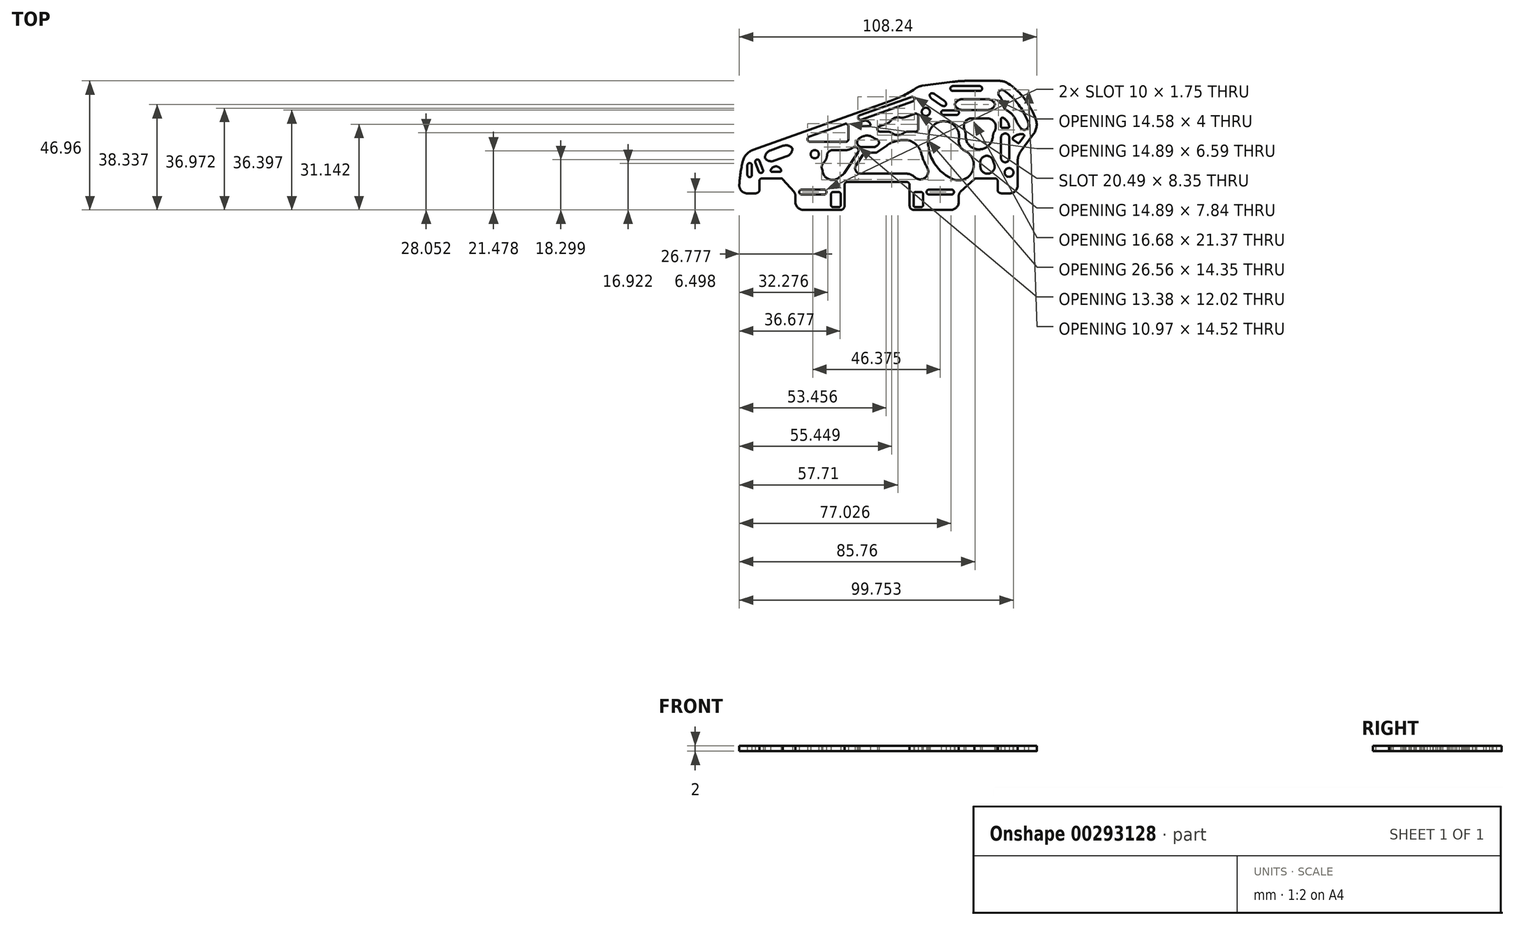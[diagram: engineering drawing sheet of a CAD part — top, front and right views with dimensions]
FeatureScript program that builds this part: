
annotation { "Feature Type Name" : "Feature", "Feature Type Description" : "" }
export const myFeature = defineFeature(function(context is Context, id is Id, definition is map)
    precondition{}
    {
        {
            var Q0;
            Q0=qCreatedBy(makeId("Top.planeOp"),FACE);
            var sketch = newSketch(context, id + "F0", { "sketchPlane" : qUnion([Q0])});
            skArc(sketch, "E0", {"start": v(29.13, 23.48) * mm, "mid": v(26.3, 23.4) * mm, "end": v(23.48, 23.12) * mm});
            skLineSegment(sketch, "E1", {"start": v(0.85, 16.15) * mm, "end": v(-49.03, -1.6) * mm});
            skArc(sketch, "E2", {"start": v(-49.03, -1.6) * mm, "mid": v(-51.49, -3.25) * mm, "end": v(-52.86, -5.87) * mm});
            skArc(sketch, "E3", {"start": v(-52.86, -5.87) * mm, "mid": v(-53.67, -10.05) * mm, "end": v(-54.12, -14.3) * mm});
            skArc(sketch, "E4", {"start": v(-54.12, -14.3) * mm, "mid": v(-53.31, -16.53) * mm, "end": v(-51.12, -17.48) * mm});
            skLineSegment(sketch, "E5", {"start": v(-51.12, -17.48) * mm, "end": v(-48.44, -17.48) * mm});
            skArc(sketch, "E6", {"start": v(-48.44, -17.48) * mm, "mid": v(-47.78, -17.37) * mm, "end": v(-47.2, -17.05) * mm});
            skArc(sketch, "E7", {"start": v(-47.2, -17.05) * mm, "mid": v(-46.92, -16.7) * mm, "end": v(-46.82, -16.27) * mm});
            skLineSegment(sketch, "E8", {"start": v(-46.82, -16.27) * mm, "end": v(-46.82, -12.98) * mm});
            skArc(sketch, "E9", {"start": v(-45.82, -11.98) * mm, "mid": v(-46.53, -12.27) * mm, "end": v(-46.82, -12.98) * mm});
            skLineSegment(sketch, "E10", {"start": v(-45.82, -11.98) * mm, "end": v(-39.02, -11.98) * mm});
            skArc(sketch, "E11", {"start": v(-38.23, -12.37) * mm, "mid": v(-38.58, -12.08) * mm, "end": v(-39.02, -11.98) * mm});
            skArc(sketch, "E12", {"start": v(-33.72, -20.48) * mm, "mid": v(-32.84, -22.6) * mm, "end": v(-30.72, -23.48) * mm});
            skLineSegment(sketch, "E13", {"start": v(-30.72, -23.48) * mm, "end": v(-17.32, -23.48) * mm});
            skArc(sketch, "E14", {"start": v(22.78, -23.48) * mm, "mid": v(24.9, -22.6) * mm, "end": v(25.78, -20.48) * mm});
            skLineSegment(sketch, "E15", {"start": v(25.78, -20.48) * mm, "end": v(25.78, -18.36) * mm});
            skArc(sketch, "E16", {"start": v(32.11, -11.98) * mm, "mid": v(31.73, -12.06) * mm, "end": v(31.4, -12.27) * mm});
            skLineSegment(sketch, "E17", {"start": v(32.11, -11.98) * mm, "end": v(38.91, -11.98) * mm});
            skArc(sketch, "E18", {"start": v(39.91, -12.98) * mm, "mid": v(39.62, -12.27) * mm, "end": v(38.91, -11.98) * mm});
            skLineSegment(sketch, "E19", {"start": v(39.91, -12.98) * mm, "end": v(39.91, -16.65) * mm});
            skArc(sketch, "E20", {"start": v(39.91, -16.65) * mm, "mid": v(40.62, -17.26) * mm, "end": v(41.53, -17.48) * mm});
            skLineSegment(sketch, "E21", {"start": v(41.53, -17.48) * mm, "end": v(44.2, -17.48) * mm});
            skArc(sketch, "E22", {"start": v(44.2, -17.48) * mm, "mid": v(46.32, -16.6) * mm, "end": v(47.2, -14.48) * mm});
            skLineSegment(sketch, "E23", {"start": v(47.2, -14.48) * mm, "end": v(47.2, -5.72) * mm});
            skArc(sketch, "E24", {"start": v(-47.04, -9.52) * mm, "mid": v(-45.98, -10) * mm, "end": v(-45.5, -8.94) * mm});
            skLineSegment(sketch, "E25", {"start": v(-48.27, -6.25) * mm, "end": v(-47.04, -9.52) * mm});
            skArc(sketch, "E26", {"start": v(-46.73, -5.66) * mm, "mid": v(-47.8, -5.18) * mm, "end": v(-48.27, -6.25) * mm});
            skLineSegment(sketch, "E27", {"start": v(-45.5, -8.94) * mm, "end": v(-46.73, -5.66) * mm});
            skCircle(sketch, "E28", {"center": v(-26.66, -3.2) * mm, "radius": 1.5 * mm});
            skCircle(sketch, "E29", {"center": v(13.78, 12.22) * mm, "radius": 1.5 * mm});
            skArc(sketch, "E30", {"start": v(-34.78, -1.3) * mm, "mid": v(-34.81, -1.1) * mm, "end": v(-34.92, -0.92) * mm});
            skArc(sketch, "E31", {"start": v(-36.77, -3.92) * mm, "mid": v(-35.39, -2.9) * mm, "end": v(-34.78, -1.3) * mm});
            skLineSegment(sketch, "E32", {"start": v(-41.48, -5.6) * mm, "end": v(-36.77, -3.92) * mm});
            skArc(sketch, "E33", {"start": v(-44.68, -4.82) * mm, "mid": v(-43.2, -5.69) * mm, "end": v(-41.48, -5.6) * mm});
            skArc(sketch, "E34", {"start": v(-44.8, -4.44) * mm, "mid": v(-44.78, -4.65) * mm, "end": v(-44.68, -4.82) * mm});
            skArc(sketch, "E35", {"start": v(-42.82, -1.83) * mm, "mid": v(-44.2, -2.84) * mm, "end": v(-44.8, -4.44) * mm});
            skLineSegment(sketch, "E36", {"start": v(-38.11, -0.15) * mm, "end": v(-42.82, -1.83) * mm});
            skArc(sketch, "E37", {"start": v(-34.92, -0.92) * mm, "mid": v(-36.4, -0.06) * mm, "end": v(-38.11, -0.15) * mm});
            skLineSegment(sketch, "E38", {"start": v(27.14, 12.86) * mm, "end": v(36.14, 12.86) * mm});
            skArc(sketch, "E39", {"start": v(24.4, 14.66) * mm, "mid": v(25.5, 13.35) * mm, "end": v(27.14, 12.86) * mm});
            skArc(sketch, "E40", {"start": v(24.4, 15.06) * mm, "mid": v(24.35, 14.86) * mm, "end": v(24.4, 14.66) * mm});
            skArc(sketch, "E41", {"start": v(27.14, 16.86) * mm, "mid": v(25.5, 16.37) * mm, "end": v(24.4, 15.06) * mm});
            skLineSegment(sketch, "E42", {"start": v(36.14, 16.86) * mm, "end": v(27.14, 16.86) * mm});
            skArc(sketch, "E43", {"start": v(38.89, 15.06) * mm, "mid": v(37.78, 16.37) * mm, "end": v(36.14, 16.86) * mm});
            skArc(sketch, "E44", {"start": v(38.89, 14.66) * mm, "mid": v(38.93, 14.86) * mm, "end": v(38.89, 15.06) * mm});
            skArc(sketch, "E45", {"start": v(36.14, 12.86) * mm, "mid": v(37.78, 13.35) * mm, "end": v(38.89, 14.66) * mm});
            skArc(sketch, "E46", {"start": v(-15.4, 1.28) * mm, "mid": v(-14.7, 1.57) * mm, "end": v(-14.4, 2.28) * mm});
            skLineSegment(sketch, "E47", {"start": v(-28.3, 1.28) * mm, "end": v(-15.4, 1.28) * mm});
            skArc(sketch, "E48", {"start": v(-28.64, 3.22) * mm, "mid": v(-29.29, 2.1) * mm, "end": v(-28.3, 1.28) * mm});
            skLineSegment(sketch, "E49", {"start": v(-15.74, 7.81) * mm, "end": v(-28.64, 3.22) * mm});
            skArc(sketch, "E50", {"start": v(-14.4, 6.87) * mm, "mid": v(-14.82, 7.69) * mm, "end": v(-15.74, 7.81) * mm});
            skLineSegment(sketch, "E51", {"start": v(-14.4, 2.28) * mm, "end": v(-14.4, 6.87) * mm});
            skLineSegment(sketch, "E52", {"start": v(-19.97, -22.48) * mm, "end": v(-17.97, -22.48) * mm});
            skArc(sketch, "E53", {"start": v(-20.72, -21.73) * mm, "mid": v(-20.5, -22.26) * mm, "end": v(-19.97, -22.48) * mm});
            skLineSegment(sketch, "E54", {"start": v(-20.72, -17.73) * mm, "end": v(-20.72, -21.73) * mm});
            skArc(sketch, "E55", {"start": v(-19.97, -16.98) * mm, "mid": v(-20.5, -17.2) * mm, "end": v(-20.72, -17.73) * mm});
            skLineSegment(sketch, "E56", {"start": v(-17.97, -16.98) * mm, "end": v(-19.97, -16.98) * mm});
            skArc(sketch, "E57", {"start": v(-17.22, -17.73) * mm, "mid": v(-17.44, -17.2) * mm, "end": v(-17.97, -16.98) * mm});
            skLineSegment(sketch, "E58", {"start": v(-17.22, -21.73) * mm, "end": v(-17.22, -17.73) * mm});
            skArc(sketch, "E59", {"start": v(-17.97, -22.48) * mm, "mid": v(-17.44, -22.26) * mm, "end": v(-17.22, -21.73) * mm});
            skArc(sketch, "E60", {"start": v(14.9, -16.1) * mm, "mid": v(14.03, -16.98) * mm, "end": v(14.9, -17.86) * mm});
            skLineSegment(sketch, "E61", {"start": v(23.16, -16.1) * mm, "end": v(14.9, -16.1) * mm});
            skArc(sketch, "E62", {"start": v(23.16, -17.86) * mm, "mid": v(24.03, -16.98) * mm, "end": v(23.16, -16.1) * mm});
            skLineSegment(sketch, "E63", {"start": v(14.9, -17.86) * mm, "end": v(23.16, -17.86) * mm});
            skArc(sketch, "E64", {"start": v(-31.47, -16.1) * mm, "mid": v(-32.34, -16.98) * mm, "end": v(-31.47, -17.86) * mm});
            skLineSegment(sketch, "E65", {"start": v(-23.22, -16.1) * mm, "end": v(-31.47, -16.1) * mm});
            skArc(sketch, "E66", {"start": v(-23.22, -17.86) * mm, "mid": v(-22.34, -16.98) * mm, "end": v(-23.22, -16.1) * mm});
            skLineSegment(sketch, "E67", {"start": v(-31.47, -17.86) * mm, "end": v(-23.22, -17.86) * mm});
            skCircle(sketch, "E68", {"center": v(44.08, -9.86) * mm, "radius": 1.6 * mm});
            skLineSegment(sketch, "E69", {"start": v(6.78, -13.3) * mm, "end": v(-14.72, -13.3) * mm});
            skArc(sketch, "E70", {"start": v(7.88, -14.4) * mm, "mid": v(7.56, -13.63) * mm, "end": v(6.78, -13.3) * mm});
            skArc(sketch, "E71", {"start": v(-14.72, -13.3) * mm, "mid": v(-15.5, -13.63) * mm, "end": v(-15.82, -14.4) * mm});
            skLineSegment(sketch, "E72", {"start": v(10.03, -22.48) * mm, "end": v(12.03, -22.48) * mm});
            skArc(sketch, "E73", {"start": v(9.28, -21.73) * mm, "mid": v(9.5, -22.26) * mm, "end": v(10.03, -22.48) * mm});
            skLineSegment(sketch, "E74", {"start": v(9.28, -17.73) * mm, "end": v(9.28, -21.73) * mm});
            skArc(sketch, "E75", {"start": v(10.03, -16.98) * mm, "mid": v(9.5, -17.2) * mm, "end": v(9.28, -17.73) * mm});
            skLineSegment(sketch, "E76", {"start": v(12.03, -16.98) * mm, "end": v(10.03, -16.98) * mm});
            skArc(sketch, "E77", {"start": v(12.78, -17.73) * mm, "mid": v(12.56, -17.2) * mm, "end": v(12.03, -16.98) * mm});
            skLineSegment(sketch, "E78", {"start": v(12.78, -21.73) * mm, "end": v(12.78, -17.73) * mm});
            skArc(sketch, "E79", {"start": v(12.03, -22.48) * mm, "mid": v(12.56, -22.26) * mm, "end": v(12.78, -21.73) * mm});
            skLineSegment(sketch, "E80", {"start": v(41.64, 6.36) * mm, "end": v(43.6, 6.36) * mm});
            skArc(sketch, "E81", {"start": v(41.14, 6.86) * mm, "mid": v(41.29, 6.5) * mm, "end": v(41.64, 6.36) * mm});
            skLineSegment(sketch, "E82", {"start": v(41.14, 9.62) * mm, "end": v(41.14, 6.86) * mm});
            skArc(sketch, "E83", {"start": v(41.87, 10.07) * mm, "mid": v(41.38, 10.05) * mm, "end": v(41.14, 9.62) * mm});
            skArc(sketch, "E84", {"start": v(44.1, 6.92) * mm, "mid": v(43.37, 8.77) * mm, "end": v(41.87, 10.07) * mm});
            skArc(sketch, "E85", {"start": v(43.6, 6.36) * mm, "mid": v(43.98, 6.53) * mm, "end": v(44.1, 6.92) * mm});
            skLineSegment(sketch, "E86", {"start": v(41.14, 2.86) * mm, "end": v(41.14, -4.64) * mm});
            skArc(sketch, "E87", {"start": v(44.14, 2.86) * mm, "mid": v(42.64, 4.36) * mm, "end": v(41.14, 2.86) * mm});
            skLineSegment(sketch, "E88", {"start": v(44.14, -4.64) * mm, "end": v(44.14, 2.86) * mm});
            skArc(sketch, "E89", {"start": v(41.14, -4.64) * mm, "mid": v(42.64, -6.14) * mm, "end": v(44.14, -4.64) * mm});
            skLineSegment(sketch, "E90", {"start": v(-9.8, 9.36) * mm, "end": v(9.03, 16.07) * mm});
            skArc(sketch, "E91", {"start": v(-10.36, 10.92) * mm, "mid": v(-10.86, 9.86) * mm, "end": v(-9.8, 9.36) * mm});
            skLineSegment(sketch, "E92", {"start": v(8.48, 17.62) * mm, "end": v(-10.36, 10.92) * mm});
            skArc(sketch, "E93", {"start": v(9.03, 16.07) * mm, "mid": v(9.53, 17.12) * mm, "end": v(8.48, 17.62) * mm});
            skLineSegment(sketch, "E94", {"start": v(23.58, 19.82) * mm, "end": v(33.38, 19.82) * mm});
            skLineSegment(sketch, "E95", {"start": v(33.38, 21.57) * mm, "end": v(23.58, 21.57) * mm});
            skLineSegment(sketch, "E96", {"start": v(7.33, 5) * mm, "end": v(10.03, 5) * mm});
            skArc(sketch, "E97", {"start": v(-3.2, 6.94) * mm, "mid": v(-3.85, 5.82) * mm, "end": v(-2.87, 5) * mm});
            skLineSegment(sketch, "E98", {"start": v(9.7, 11.53) * mm, "end": v(6.07, 10.24) * mm});
            skArc(sketch, "E99", {"start": v(11.03, 10.59) * mm, "mid": v(10.61, 11.4) * mm, "end": v(9.7, 11.53) * mm});
            skLineSegment(sketch, "E100", {"start": v(11.03, 6) * mm, "end": v(11.03, 10.59) * mm});
            skArc(sketch, "E101", {"start": v(10.03, 5) * mm, "mid": v(10.74, 5.29) * mm, "end": v(11.03, 6) * mm});
            skLineSegment(sketch, "E102", {"start": v(-38.23, -12.37) * mm, "end": v(-34.22, -16.91) * mm});
            skLineSegment(sketch, "E103", {"start": v(-33.72, -18.24) * mm, "end": v(-33.72, -20.48) * mm});
            skArc(sketch, "E104", {"start": v(-33.72, -18.24) * mm, "mid": v(-33.85, -17.53) * mm, "end": v(-34.22, -16.91) * mm});
            skLineSegment(sketch, "E105", {"start": v(31.4, -12.27) * mm, "end": v(26.42, -16.89) * mm});
            skArc(sketch, "E106", {"start": v(26.42, -16.89) * mm, "mid": v(25.95, -17.55) * mm, "end": v(25.78, -18.36) * mm});
            skArc(sketch, "E107", {"start": v(-51.18, -10.74) * mm, "mid": v(-50.35, -11.56) * mm, "end": v(-49.53, -10.74) * mm});
            skLineSegment(sketch, "E108", {"start": v(-49.53, -7.24) * mm, "end": v(-49.53, -10.74) * mm});
            skArc(sketch, "E109", {"start": v(-49.53, -7.24) * mm, "mid": v(-50.35, -6.41) * mm, "end": v(-51.18, -7.24) * mm});
            skLineSegment(sketch, "E110", {"start": v(-51.18, -10.74) * mm, "end": v(-51.18, -7.24) * mm});
            skLineSegment(sketch, "E111", {"start": v(-15.82, -14.4) * mm, "end": v(-15.82, -21.98) * mm});
            skArc(sketch, "E112", {"start": v(-17.32, -23.48) * mm, "mid": v(-16.26, -23.04) * mm, "end": v(-15.82, -21.98) * mm});
            skLineSegment(sketch, "E113", {"start": v(7.88, -21.98) * mm, "end": v(7.88, -14.4) * mm});
            skLineSegment(sketch, "E114", {"start": v(9.38, -23.48) * mm, "end": v(22.78, -23.48) * mm});
            skArc(sketch, "E115", {"start": v(7.88, -21.98) * mm, "mid": v(8.32, -23.04) * mm, "end": v(9.38, -23.48) * mm});
            skLineSegment(sketch, "E116", {"start": v(23.48, 23.12) * mm, "end": v(12.54, 21.72) * mm});
            skArc(sketch, "E117", {"start": v(0.85, 16.15) * mm, "mid": v(5.78, 18.25) * mm, "end": v(10.42, 20.93) * mm});
            skArc(sketch, "E118", {"start": v(12.54, 21.72) * mm, "mid": v(11.43, 21.45) * mm, "end": v(10.42, 20.93) * mm});
            skLineSegment(sketch, "E119", {"start": v(52.6, 12.21) * mm, "end": v(53.56, 10.14) * mm});
            skArc(sketch, "E120", {"start": v(48.37, -2.16) * mm, "mid": v(47.5, -3.84) * mm, "end": v(47.2, -5.72) * mm});
            skArc(sketch, "E121", {"start": v(52.6, 12.21) * mm, "mid": v(48.93, 17.92) * mm, "end": v(43.88, 22.44) * mm});
            skLineSegment(sketch, "E122", {"start": v(40.51, 23.48) * mm, "end": v(29.13, 23.48) * mm});
            skArc(sketch, "E123", {"start": v(43.88, 22.44) * mm, "mid": v(42.28, 23.22) * mm, "end": v(40.51, 23.48) * mm});
            skLineSegment(sketch, "E124", {"start": v(52.95, 4.04) * mm, "end": v(48.37, -2.16) * mm});
            skArc(sketch, "E125", {"start": v(52.95, 4.04) * mm, "mid": v(54.1, 7) * mm, "end": v(53.56, 10.14) * mm});
            skArc(sketch, "E126", {"start": v(49.88, 10.94) * mm, "mid": v(46.65, 15.97) * mm, "end": v(42.2, 19.96) * mm});
            skArc(sketch, "E127", {"start": v(42.2, 19.96) * mm, "mid": v(40.46, 19.73) * mm, "end": v(40.5, 17.97) * mm});
            skArc(sketch, "E128", {"start": v(41.64, 16.26) * mm, "mid": v(41.15, 17.16) * mm, "end": v(40.5, 17.97) * mm});
            skArc(sketch, "E129", {"start": v(41.93, 14.86) * mm, "mid": v(41.86, 15.57) * mm, "end": v(41.64, 16.26) * mm});
            skArc(sketch, "E130", {"start": v(41.93, 14.86) * mm, "mid": v(42.28, 13.62) * mm, "end": v(43.23, 12.74) * mm});
            skArc(sketch, "E131", {"start": v(46.58, 9.13) * mm, "mid": v(45.23, 11.23) * mm, "end": v(43.23, 12.74) * mm});
            skArc(sketch, "E132", {"start": v(46.58, 9.13) * mm, "mid": v(47.43, 7.53) * mm, "end": v(48.55, 6.1) * mm});
            skArc(sketch, "E133", {"start": v(48.55, 6.1) * mm, "mid": v(49.9, 5.69) * mm, "end": v(50.96, 6.62) * mm});
            skArc(sketch, "E134", {"start": v(50.96, 6.62) * mm, "mid": v(51.12, 7.76) * mm, "end": v(50.84, 8.87) * mm});
            skLineSegment(sketch, "E135", {"start": v(49.88, 10.94) * mm, "end": v(50.84, 8.87) * mm});
            skArc(sketch, "E136", {"start": v(49.16, 4.05) * mm, "mid": v(47.18, 3.9) * mm, "end": v(45.5, 2.85) * mm});
            skArc(sketch, "E137", {"start": v(49.48, 3.26) * mm, "mid": v(49.54, 3.74) * mm, "end": v(49.16, 4.05) * mm});
            skLineSegment(sketch, "E138", {"start": v(47.84, 1.03) * mm, "end": v(49.48, 3.26) * mm});
            skArc(sketch, "E139", {"start": v(47.14, 0.93) * mm, "mid": v(47.51, 0.84) * mm, "end": v(47.84, 1.03) * mm});
            skLineSegment(sketch, "E140", {"start": v(45.56, 2.1) * mm, "end": v(47.14, 0.93) * mm});
            skArc(sketch, "E141", {"start": v(45.5, 2.85) * mm, "mid": v(45.36, 2.46) * mm, "end": v(45.56, 2.1) * mm});
            skArc(sketch, "E142", {"start": v(23.58, 21.57) * mm, "mid": v(22.7, 20.7) * mm, "end": v(23.58, 19.82) * mm});
            skArc(sketch, "E143", {"start": v(33.38, 19.82) * mm, "mid": v(34.26, 20.7) * mm, "end": v(33.38, 21.57) * mm});
            skArc(sketch, "E144", {"start": v(30.45, 9.86) * mm, "mid": v(28.1, 8.63) * mm, "end": v(27.79, 6) * mm});
            skLineSegment(sketch, "E145", {"start": v(36.14, 9.86) * mm, "end": v(30.45, 9.86) * mm});
            skArc(sketch, "E146", {"start": v(38.78, 5.18) * mm, "mid": v(38.83, 8.29) * mm, "end": v(36.14, 9.86) * mm});
            skArc(sketch, "E147", {"start": v(38.78, 5.18) * mm, "mid": v(38.35, 4.23) * mm, "end": v(38.15, 3.2) * mm});
            skArc(sketch, "E148", {"start": v(30.24, -0.54) * mm, "mid": v(35.28, -0.97) * mm, "end": v(38.15, 3.2) * mm});
            skArc(sketch, "E149", {"start": v(28.31, 3.17) * mm, "mid": v(28.82, 1.08) * mm, "end": v(30.24, -0.54) * mm});
            skArc(sketch, "E150", {"start": v(28.31, 3.17) * mm, "mid": v(28.18, 4.61) * mm, "end": v(27.79, 6) * mm});
            skArc(sketch, "E151", {"start": v(38.25, -5.64) * mm, "mid": v(35.6, -3.83) * mm, "end": v(33.62, -6.37) * mm});
            skArc(sketch, "E152", {"start": v(38.25, -5.64) * mm, "mid": v(38.39, -6.12) * mm, "end": v(38.58, -6.58) * mm});
            skArc(sketch, "E153", {"start": v(33.64, -7.55) * mm, "mid": v(36.73, -10.25) * mm, "end": v(38.58, -6.58) * mm});
            skArc(sketch, "E154", {"start": v(33.64, -7.55) * mm, "mid": v(33.65, -6.96) * mm, "end": v(33.62, -6.37) * mm});
            skArc(sketch, "E155", {"start": v(-10.96, -2.6) * mm, "mid": v(-11.17, -0.89) * mm, "end": v(-12.9, -0.84) * mm});
            skLineSegment(sketch, "E156", {"start": v(-15.99, -10.16) * mm, "end": v(-10.96, -2.6) * mm});
            skArc(sketch, "E157", {"start": v(-16.69, -10.81) * mm, "mid": v(-16.3, -10.53) * mm, "end": v(-15.99, -10.16) * mm});
            skArc(sketch, "E158", {"start": v(-16.69, -10.81) * mm, "mid": v(-17.18, -11.13) * mm, "end": v(-17.62, -11.5) * mm});
            skArc(sketch, "E159", {"start": v(-23.79, -9.47) * mm, "mid": v(-21.33, -12.39) * mm, "end": v(-17.62, -11.5) * mm});
            skFitSpline(sketch, "E160", {"points": [v(-24.02, -8.54) * mm, v(-23.91, -8.84) * mm, v(-23.84, -9.15) * mm, v(-23.79, -9.47) * mm]});
            skArc(sketch, "E161", {"start": v(-23.53, -6.44) * mm, "mid": v(-24.08, -7.42) * mm, "end": v(-24.02, -8.54) * mm});
            skArc(sketch, "E162", {"start": v(-23.53, -6.44) * mm, "mid": v(-22.59, -5.12) * mm, "end": v(-22.17, -3.56) * mm});
            skArc(sketch, "E163", {"start": v(-20.18, -1.72) * mm, "mid": v(-21.54, -2.25) * mm, "end": v(-22.17, -3.56) * mm});
            skLineSegment(sketch, "E164", {"start": v(-15.4, -1.72) * mm, "end": v(-20.18, -1.72) * mm});
            skArc(sketch, "E165", {"start": v(-15.4, -1.72) * mm, "mid": v(-14.07, -1.5) * mm, "end": v(-12.9, -0.84) * mm});
            skArc(sketch, "E166", {"start": v(5.96, 2) * mm, "mid": v(2.58, 1.47) * mm, "end": v(-0.49, -0.06) * mm});
            skArc(sketch, "E167", {"start": v(12.1, -2.81) * mm, "mid": v(9.85, 0.65) * mm, "end": v(5.96, 2) * mm});
            skArc(sketch, "E168", {"start": v(12.1, -2.81) * mm, "mid": v(12.96, -5.45) * mm, "end": v(14.23, -7.93) * mm});
            skArc(sketch, "E169", {"start": v(9.68, -11.5) * mm, "mid": v(13.54, -11.74) * mm, "end": v(14.23, -7.93) * mm});
            skArc(sketch, "E170", {"start": v(9.68, -11.5) * mm, "mid": v(8.35, -10.62) * mm, "end": v(6.78, -10.3) * mm});
            skLineSegment(sketch, "E171", {"start": v(-9.95, -10.3) * mm, "end": v(6.78, -10.3) * mm});
            skArc(sketch, "E172", {"start": v(-11.62, -7.2) * mm, "mid": v(-11.72, -9.25) * mm, "end": v(-9.95, -10.3) * mm});
            skLineSegment(sketch, "E173", {"start": v(-9.16, -3.49) * mm, "end": v(-11.62, -7.2) * mm});
            skArc(sketch, "E174", {"start": v(-7.5, -2.6) * mm, "mid": v(-8.44, -2.83) * mm, "end": v(-9.16, -3.49) * mm});
            skLineSegment(sketch, "E175", {"start": v(-4.23, -2.6) * mm, "end": v(-7.5, -2.6) * mm});
            skArc(sketch, "E176", {"start": v(-4.23, -2.6) * mm, "mid": v(-4.08, -2.57) * mm, "end": v(-3.94, -2.5) * mm});
            skLineSegment(sketch, "E177", {"start": v(-0.49, -0.06) * mm, "end": v(-3.94, -2.5) * mm});
            skArc(sketch, "E178", {"start": v(21.14, 15.28) * mm, "mid": v(20.85, 15.86) * mm, "end": v(20.38, 16.31) * mm});
            skLineSegment(sketch, "E179", {"start": v(17.1, 18.6) * mm, "end": v(20.38, 16.31) * mm});
            skArc(sketch, "E180", {"start": v(17.1, 18.6) * mm, "mid": v(16.52, 18.89) * mm, "end": v(15.87, 18.97) * mm});
            skArc(sketch, "E181", {"start": v(15.87, 18.97) * mm, "mid": v(15.3, 18.65) * mm, "end": v(15.2, 18) * mm});
            skArc(sketch, "E182", {"start": v(15.2, 18) * mm, "mid": v(15.5, 17.42) * mm, "end": v(15.96, 16.97) * mm});
            skLineSegment(sketch, "E183", {"start": v(19.24, 14.67) * mm, "end": v(15.96, 16.97) * mm});
            skArc(sketch, "E184", {"start": v(19.24, 14.67) * mm, "mid": v(19.82, 14.4) * mm, "end": v(20.47, 14.31) * mm});
            skArc(sketch, "E185", {"start": v(20.47, 14.31) * mm, "mid": v(21.04, 14.63) * mm, "end": v(21.14, 15.28) * mm});
            skArc(sketch, "E186", {"start": v(14.8, 4.14) * mm, "mid": v(16.27, -5.45) * mm, "end": v(23.28, -12.17) * mm});
            skArc(sketch, "E187", {"start": v(25.83, 2.2) * mm, "mid": v(21.28, 8.68) * mm, "end": v(14.8, 4.14) * mm});
            skArc(sketch, "E188", {"start": v(25.83, 2.2) * mm, "mid": v(26.2, -0.28) * mm, "end": v(28.02, -2.02) * mm});
            skArc(sketch, "E189", {"start": v(23.28, -12.17) * mm, "mid": v(30.73, -9.46) * mm, "end": v(28.02, -2.02) * mm});
            skArc(sketch, "E190", {"start": v(-5.2, 2.74) * mm, "mid": v(-8.07, 3.53) * mm, "end": v(-10.76, 2.24) * mm});
            skArc(sketch, "E191", {"start": v(-5.2, 2.74) * mm, "mid": v(-4.67, 2.42) * mm, "end": v(-4.1, 2.19) * mm});
            skArc(sketch, "E192", {"start": v(-3.77, 0.07) * mm, "mid": v(-3.28, 1.23) * mm, "end": v(-4.1, 2.19) * mm});
            skLineSegment(sketch, "E193", {"start": v(-4.58, -0.5) * mm, "end": v(-3.77, 0.07) * mm});
            skArc(sketch, "E194", {"start": v(-4.87, -0.6) * mm, "mid": v(-4.72, -0.57) * mm, "end": v(-4.58, -0.5) * mm});
            skLineSegment(sketch, "E195", {"start": v(-9.56, -0.6) * mm, "end": v(-4.87, -0.6) * mm});
            skArc(sketch, "E196", {"start": v(-10.76, 2.24) * mm, "mid": v(-11.1, 0.43) * mm, "end": v(-9.56, -0.6) * mm});
            skArc(sketch, "E197", {"start": v(24.98, 11.09) * mm, "mid": v(25.83, 11.94) * mm, "end": v(24.98, 12.79) * mm});
            skLineSegment(sketch, "E198", {"start": v(24.98, 12.79) * mm, "end": v(20.18, 12.79) * mm});
            skArc(sketch, "E199", {"start": v(20.18, 12.79) * mm, "mid": v(19.33, 11.94) * mm, "end": v(20.18, 11.09) * mm});
            skLineSegment(sketch, "E200", {"start": v(20.18, 11.09) * mm, "end": v(24.98, 11.09) * mm});
            skArc(sketch, "E201", {"start": v(-38.9, -8.97) * mm, "mid": v(-40.78, -7.63) * mm, "end": v(-42.66, -8.97) * mm});
            skArc(sketch, "E202", {"start": v(-39.36, -9.63) * mm, "mid": v(-38.95, -9.42) * mm, "end": v(-38.9, -8.97) * mm});
            skLineSegment(sketch, "E203", {"start": v(-39.36, -9.63) * mm, "end": v(-42.2, -9.63) * mm});
            skArc(sketch, "E204", {"start": v(-42.66, -8.97) * mm, "mid": v(-42.6, -9.42) * mm, "end": v(-42.2, -9.63) * mm});
            skLineSegment(sketch, "E205", {"start": v(-6.88, 7.04) * mm, "end": v(-9.71, 7.04) * mm});
            skArc(sketch, "E206", {"start": v(-10.18, 7.7) * mm, "mid": v(-10.12, 7.25) * mm, "end": v(-9.71, 7.04) * mm});
            skArc(sketch, "E207", {"start": v(-6.41, 7.7) * mm, "mid": v(-8.3, 9.04) * mm, "end": v(-10.18, 7.7) * mm});
            skArc(sketch, "E208", {"start": v(-6.88, 7.04) * mm, "mid": v(-6.47, 7.25) * mm, "end": v(-6.41, 7.7) * mm});
            skLineSegment(sketch, "E209", {"start": v(-0.4, 7.93) * mm, "end": v(-3.2, 6.94) * mm});
            skLineSegment(sketch, "E210", {"start": v(-2.87, 5) * mm, "end": v(-0.17, 5) * mm});
            skArc(sketch, "E211", {"start": v(1.63, 4.4) * mm, "mid": v(3.58, 3.74) * mm, "end": v(5.53, 4.4) * mm});
            skArc(sketch, "E212", {"start": v(4.35, 10.15) * mm, "mid": v(2.5, 10.06) * mm, "end": v(0.99, 8.95) * mm});
            skArc(sketch, "E213", {"start": v(4.35, 10.15) * mm, "mid": v(5.22, 10.07) * mm, "end": v(6.07, 10.24) * mm});
            skArc(sketch, "E214", {"start": v(-0.4, 7.93) * mm, "mid": v(0.37, 8.34) * mm, "end": v(0.99, 8.95) * mm});
            skArc(sketch, "E215", {"start": v(1.63, 4.4) * mm, "mid": v(0.78, 4.84) * mm, "end": v(-0.17, 5) * mm});
            skArc(sketch, "E216", {"start": v(7.33, 5) * mm, "mid": v(6.38, 4.84) * mm, "end": v(5.53, 4.4) * mm});
            skSolve(sketch);
        }
        {
            var Q0;
            Q0 = qSketchRegion(id + "F0", true);
            extrude(context, id + "F1", {"entities" : qUnion([Q0]), "depth" : 2 * mm});
        }
    });
